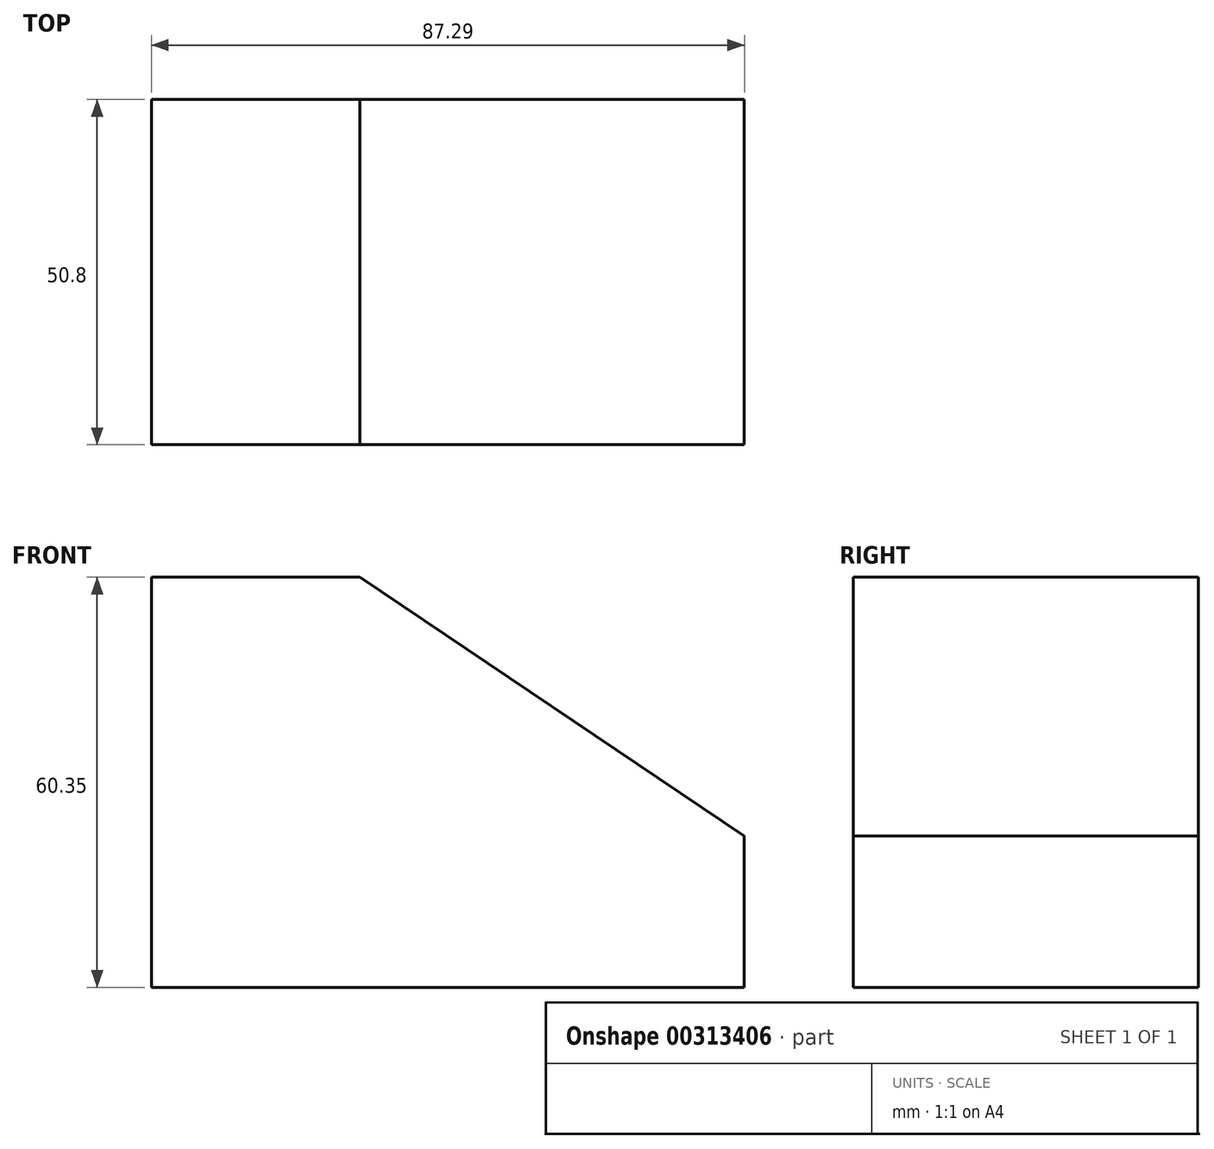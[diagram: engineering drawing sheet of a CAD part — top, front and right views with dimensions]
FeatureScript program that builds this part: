
annotation { "Feature Type Name" : "Feature", "Feature Type Description" : "" }
export const myFeature = defineFeature(function(context is Context, id is Id, definition is map)
    precondition{}
    {
        {
            var Q0;
            Q0=qCreatedBy(makeId("Front.planeOp"),FACE);
            var sketch = newSketch(context, id + "F0", { "sketchPlane" : qUnion([Q0])});
            skLineSegment(sketch, "E0", {"start": v(-46.43, 25.84) * mm, "end": v(-46.43, -34.51) * mm});
            skLineSegment(sketch, "E1", {"start": v(-46.43, -34.51) * mm, "end": v(40.86, -34.51) * mm});
            skLineSegment(sketch, "E2", {"start": v(40.86, -34.51) * mm, "end": v(40.86, -12.23) * mm});
            skLineSegment(sketch, "E3", {"start": v(40.86, -12.23) * mm, "end": v(-15.79, 25.84) * mm});
            skLineSegment(sketch, "E4", {"start": v(-15.79, 25.84) * mm, "end": v(-46.43, 25.84) * mm});
            skSolve(sketch);
        }
        {
            var Q0;
            Q0 = qSketchRegion(id + "F0", true);
            extrude(context, id + "F1", {"entities" : qUnion([Q0]), "depth" : 50.8 * mm});
        }
    });
